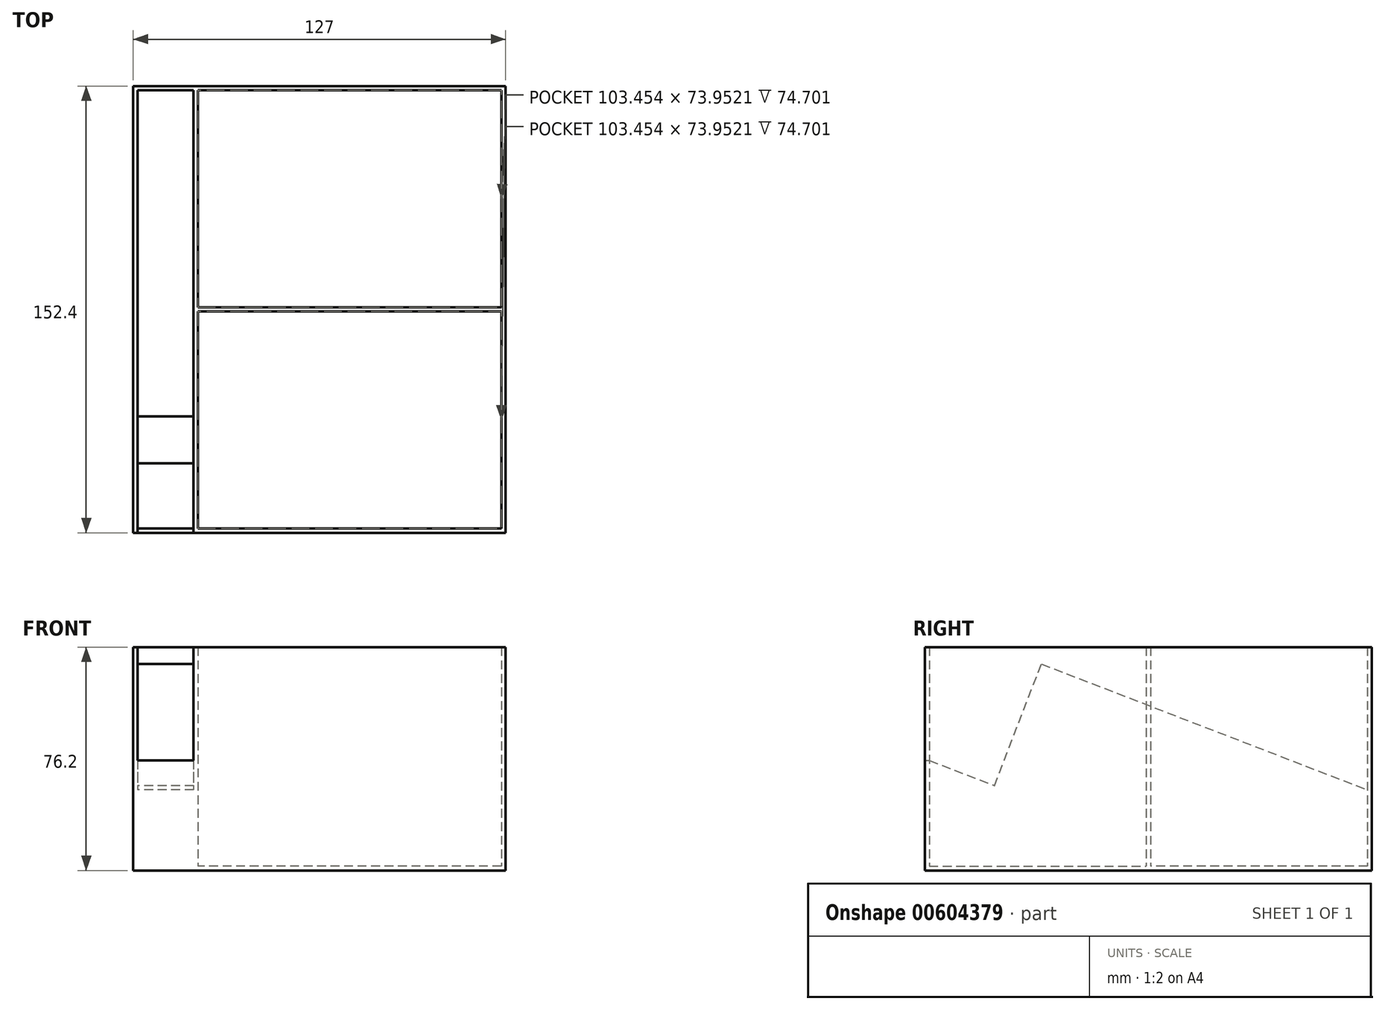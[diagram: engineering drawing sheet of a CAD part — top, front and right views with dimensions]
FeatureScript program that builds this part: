
annotation { "Feature Type Name" : "Feature", "Feature Type Description" : "" }
export const myFeature = defineFeature(function(context is Context, id is Id, definition is map)
    precondition{}
    {
        {
            var Q0;
            Q0=qCreatedBy(makeId("Top.planeOp"),FACE);
            var sketch = newSketch(context, id + "F0", { "sketchPlane" : qUnion([Q0])});
            skLineSegment(sketch, "E0.bottom", {"start": v(63.5, -76.2) * mm, "end": v(-63.5, -76.2) * mm});
            skLineSegment(sketch, "E0.top", {"start": v(63.5, 76.2) * mm, "end": v(-63.5, 76.2) * mm});
            skLineSegment(sketch, "E0.left", {"start": v(63.5, -76.2) * mm, "end": v(63.5, 76.2) * mm});
            skLineSegment(sketch, "E0.right", {"start": v(-63.5, -76.2) * mm, "end": v(-63.5, 76.2) * mm});
            skPoint(sketch, "E0.middle", {"position": v(0, 0) * mm});
            skSolve(sketch);
        }
        {
            var Q0;
            Q0=makeQuery(id+"F0.imprint","IMPRINT",FACE,{"disambiguationData":[TD([[makeQuery(id+"F0.imprint","IMPRINT",EDGE,{"derivedFrom":sQuery(id+"F0.wireOp",EDGE,"E0.bottom")}),-1.0]])]});
            extrude(context, id + "F1", {"entities" : qUnion([Q0]), "depth" : 76.2 * mm, "offsetDistance" : 25.4 * mm});
        }
        {
            var Q0;
            Q0=makeQuery(id+"F1.opExtrude","CAP_FACE",FACE,{"disambiguationData":[OSD([sQuery(id+"F0.wireOp",EDGE,"E0.bottom"),sQuery(id+"F0.wireOp",EDGE,"E0.top"),sQuery(id+"F0.wireOp",EDGE,"E0.left"),sQuery(id+"F0.wireOp",EDGE,"E0.right")])],"isStart":false});
            shell(context, id + "F2", {"entities" : qUnion([Q0]), "thickness" : 1.5 * mm});
        }
        {
            var Q0;
            Q0=makeQuery(id+"F2.opShell","OFFSET_FACE",FACE,{"disambiguationData":[OSD([sQuery(id+"F0.wireOp",EDGE,"E0.bottom"),sQuery(id+"F0.wireOp",EDGE,"E0.top"),sQuery(id+"F0.wireOp",EDGE,"E0.left"),sQuery(id+"F0.wireOp",EDGE,"E0.right")])]});
            var sketch = newSketch(context, id + "F3", { "sketchPlane" : qUnion([Q0])});
            skLineSegment(sketch, "E1.bottom", {"start": v(-42.95, 74.7) * mm, "end": v(-41.45, 74.7) * mm});
            skLineSegment(sketch, "E1.top", {"start": v(-42.95, -74.7) * mm, "end": v(-41.45, -74.7) * mm});
            skLineSegment(sketch, "E1.left", {"start": v(-42.95, 74.7) * mm, "end": v(-42.95, -74.7) * mm});
            skLineSegment(sketch, "E1.right", {"start": v(-41.45, 74.7) * mm, "end": v(-41.45, -74.7) * mm});
            skSolve(sketch);
        }
        {
            var Q0;
            Q0=qSketchRegion(id+"F3",true);
            var Q1;
            {var subQ0=sQuery(id+"F0.wireOp",EDGE,"E0.right");var subQ1=sQuery(id+"F0.wireOp",EDGE,"E0.top");Q1=makeQuery(id+"F2.opShell","OFFSET_VERTEX",VERTEX,{"disambiguationData":[OSD([subQ1,subQ0]),TDD([makeQuery(id+"F1.opExtrude","CAP_VERTEX",VERTEX,{"disambiguationData":[OSD([subQ1,subQ0])],"isStart":false})])]});}
            extrude(context, id + "F4", {"entities" : qUnion([Q0]), "operationType" : NewBodyOperationType.ADD, "endBound" : BoundingType.UP_TO_VERTEX, "depth" : 73.66 * mm, "endBoundEntityVertex" : qUnion([Q1]), "offsetDistance" : 25.4 * mm});
        }
        {
            var Q0;
            {var subQ0=sQuery(id+"F0.wireOp",EDGE,"E0.bottom");var subQ1=sQuery(id+"F0.wireOp",EDGE,"E0.top");var subQ2=sQuery(id+"F0.wireOp",EDGE,"E0.left");Q0=makeQuery(id+"F4.boolean.opBoolean","SPLIT",FACE,{"disambiguationData":[TD([makeQuery(id+"F2.opShell","OFFSET_FACE",FACE,{"disambiguationData":[OSD([subQ2])]})])],"derivedFrom":makeQuery(id+"F2.opShell","OFFSET_FACE",FACE,{"disambiguationData":[OSD([subQ0,subQ1,subQ2,sQuery(id+"F0.wireOp",EDGE,"E0.right")])]})});}
            var sketch = newSketch(context, id + "F5", { "sketchPlane" : qUnion([Q0])});
            skLineSegment(sketch, "E2", {"start": v(10.27, 74.7) * mm, "end": v(10.27, -74.7) * mm, "construction": true});
            skLineSegment(sketch, "E3", {"start": v(62, 0) * mm, "end": v(-41.45, 0) * mm, "construction": true});
            skLineSegment(sketch, "E4.bottom", {"start": v(62, -0.75) * mm, "end": v(-41.45, -0.75) * mm});
            skLineSegment(sketch, "E4.top", {"start": v(62, 0.75) * mm, "end": v(-41.45, 0.75) * mm});
            skLineSegment(sketch, "E4.left", {"start": v(62, -0.75) * mm, "end": v(62, 0.75) * mm});
            skLineSegment(sketch, "E4.right", {"start": v(-41.45, -0.75) * mm, "end": v(-41.45, 0.75) * mm});
            skPoint(sketch, "E4.middle", {"position": v(10.27, 0) * mm});
            skSolve(sketch);
        }
        {
            var Q0;
            Q0=qSketchRegion(id+"F5",true);
            var Q1;
            Q1=makeQuery(id+"F1.opExtrude","SWEPT_BODY",BODY,{"disambiguationData":[OSD([sQuery(id+"F0.wireOp",EDGE,"E0.bottom"),sQuery(id+"F0.wireOp",EDGE,"E0.top"),sQuery(id+"F0.wireOp",EDGE,"E0.left"),sQuery(id+"F0.wireOp",EDGE,"E0.right")])]});
            var Q2;
            Q2=makeQuery(id+"F4.opExtrude","CAP_VERTEX",VERTEX,{"disambiguationData":[OSD([sQuery(id+"F0.wireOp",EDGE,"E0.bottom"),sQuery(id+"F3.wireOp",EDGE,"E1.top"),sQuery(id+"F3.wireOp",EDGE,"E1.right"),dummyQuery(id+"F4.vertexPlane.planeOp",FACE)])],"isStart":false});
            extrude(context, id + "F6", {"entities" : qUnion([Q0]), "operationType" : NewBodyOperationType.ADD, "endBound" : BoundingType.UP_TO_VERTEX, "depth" : 25.4 * mm, "endBoundEntityBody" : qUnion([Q1]), "endBoundEntityVertex" : qUnion([Q2]), "offsetDistance" : 25.4 * mm});
        }
        {
            var Q0;
            Q0=makeQuery(id+"F1.opExtrude","SWEPT_FACE",FACE,{"disambiguationData":[OSD([sQuery(id+"F0.wireOp",EDGE,"E0.right")])]});
            var sketch = newSketch(context, id + "F7", { "sketchPlane" : qUnion([Q0])});
            skLineSegment(sketch, "E5", {"start": v(76.2, 38.1) * mm, "end": v(52.5, 28.95) * mm});
            skLineSegment(sketch, "E6", {"start": v(52.5, 28.95) * mm, "end": v(36.5, 70.42) * mm});
            skLineSegment(sketch, "E7", {"start": v(36.5, 70.42) * mm, "end": v(-76.2, 26.9) * mm});
            skLineSegment(sketch, "E8", {"start": v(-76.2, 26.9) * mm, "end": v(-76.2, 0) * mm});
            skLineSegment(sketch, "E9", {"start": v(-76.2, 0) * mm, "end": v(76.2, 0) * mm});
            skLineSegment(sketch, "E10", {"start": v(76.2, 0) * mm, "end": v(76.2, 38.1) * mm});
            skSolve(sketch);
        }
        {
            var Q0;
            Q0=makeQuery(id+"F7.imprint","IMPRINT",FACE,{"disambiguationData":[TD([[makeQuery(id+"F7.imprint","IMPRINT",EDGE,{"derivedFrom":sQuery(id+"F7.wireOp",EDGE,"E5")}),1.0]])]});
            var Q1;
            Q1=makeQuery(id+"F4.opExtrude","SWEPT_FACE",FACE,{"disambiguationData":[OSD([sQuery(id+"F3.wireOp",EDGE,"E1.left")])]});
            var Q2;
            Q2=makeQuery(id+"F1.opExtrude","SWEPT_BODY",BODY,{"disambiguationData":[OSD([sQuery(id+"F0.wireOp",EDGE,"E0.bottom"),sQuery(id+"F0.wireOp",EDGE,"E0.top"),sQuery(id+"F0.wireOp",EDGE,"E0.left"),sQuery(id+"F0.wireOp",EDGE,"E0.right")])]});
            extrude(context, id + "F8", {"entities" : qUnion([Q0]), "operationType" : NewBodyOperationType.ADD, "endBound" : BoundingType.UP_TO_SURFACE, "oppositeDirection" : true, "depth" : 25.4 * mm, "endBoundEntityFace" : qUnion([Q1]), "endBoundEntityBody" : qUnion([Q2]), "offsetDistance" : 25.4 * mm});
        }
        {
            var Q0;
            {var subQ0=sQuery(id+"F0.wireOp",EDGE,"E0.right");var subQ3=sQuery(id+"F0.wireOp",EDGE,"E0.bottom");Q0=makeQuery(id+"F4.boolean.opBoolean","SPLIT",FACE,{"disambiguationData":[TD([makeQuery(id+"F2.opShell","OFFSET_FACE",FACE,{"disambiguationData":[OSD([subQ0])]})])],"derivedFrom":makeQuery(id+"F2.opShell","OFFSET_FACE",FACE,{"disambiguationData":[OSD([subQ3])]})});}
            var sketch = newSketch(context, id + "F9", { "sketchPlane" : qUnion([Q0])});
            skLineSegment(sketch, "E11", {"start": v(42.95, 76.2) * mm, "end": v(42.95, 37.52) * mm});
            skLineSegment(sketch, "E12", {"start": v(42.95, 37.52) * mm, "end": v(62, 37.52) * mm});
            skLineSegment(sketch, "E13", {"start": v(62, 37.52) * mm, "end": v(62, 76.2) * mm});
            skLineSegment(sketch, "E14", {"start": v(62, 76.2) * mm, "end": v(42.95, 76.2) * mm});
            skSolve(sketch);
        }
        {
            var Q0;
            Q0=makeQuery(id+"F9.imprint","IMPRINT",FACE,{"disambiguationData":[TD([[makeQuery(id+"F9.imprint","IMPRINT",EDGE,{"derivedFrom":sQuery(id+"F9.wireOp",EDGE,"E11")}),1.0]])]});
            extrude(context, id + "F10", {"entities" : qUnion([Q0]), "operationType" : NewBodyOperationType.REMOVE, "oppositeDirection" : true, "depth" : 4.06 * mm, "offsetDistance" : 25.4 * mm});
        }
    });
